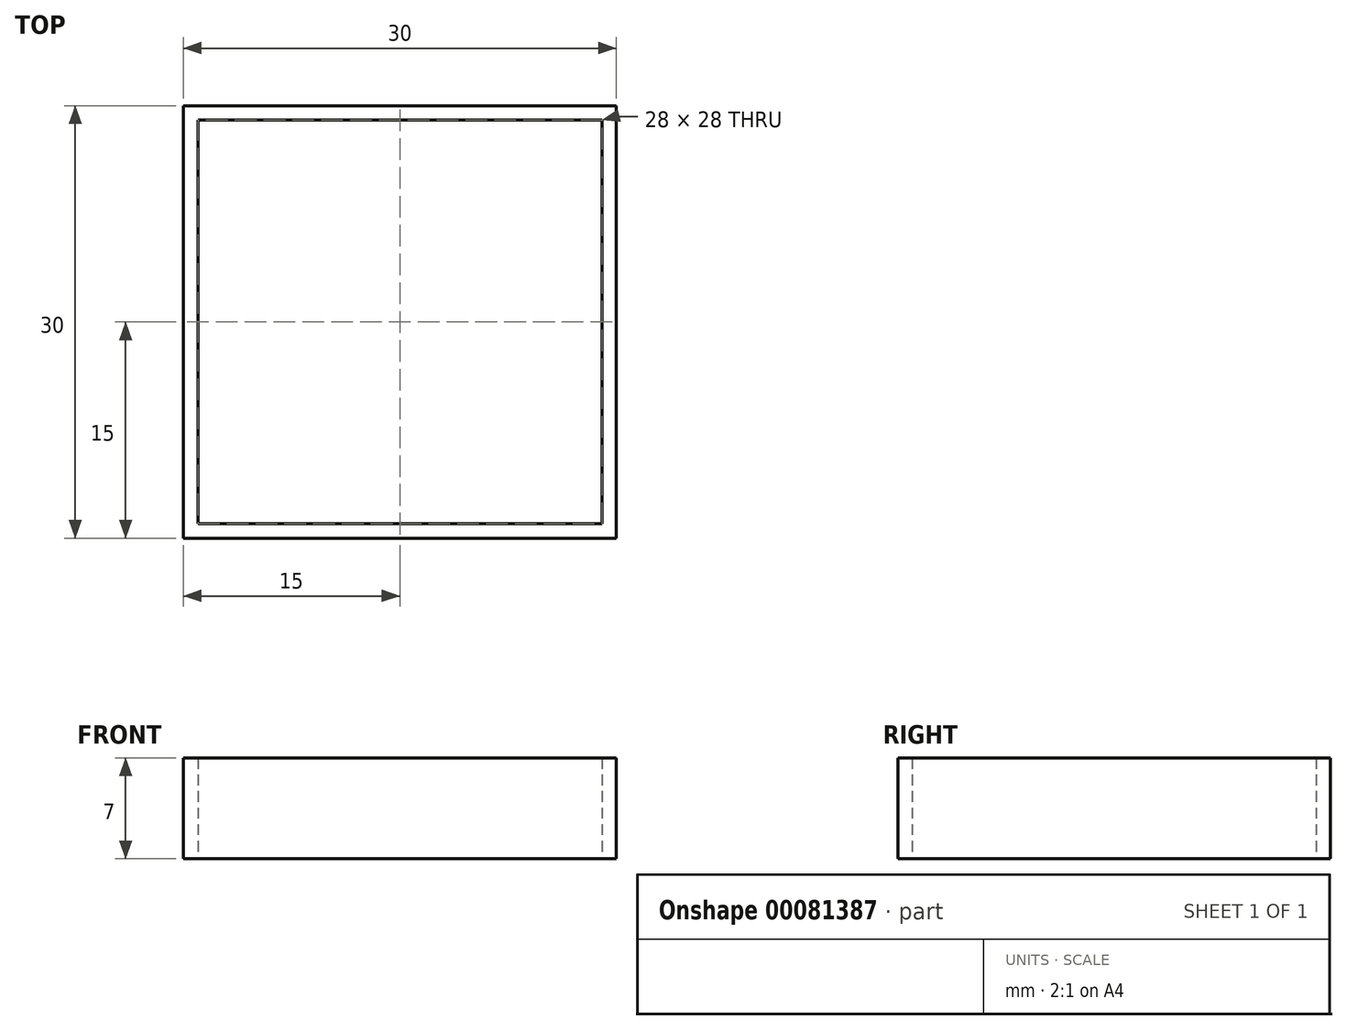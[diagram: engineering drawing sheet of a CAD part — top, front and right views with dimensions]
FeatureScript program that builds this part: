
annotation { "Feature Type Name" : "Feature", "Feature Type Description" : "" }
export const myFeature = defineFeature(function(context is Context, id is Id, definition is map)
    precondition{}
    {
        {
            var Q0;
            Q0=qCreatedBy(makeId("Top.planeOp"),FACE);
            var sketch = newSketch(context, id + "F0", { "sketchPlane" : qUnion([Q0])});
            skLineSegment(sketch, "E0.bottom", {"start": v(15, -15) * mm, "end": v(-15, -15) * mm});
            skLineSegment(sketch, "E0.top", {"start": v(15, 15) * mm, "end": v(-15, 15) * mm});
            skLineSegment(sketch, "E0.left", {"start": v(15, -15) * mm, "end": v(15, 15) * mm});
            skLineSegment(sketch, "E0.right", {"start": v(-15, -15) * mm, "end": v(-15, 15) * mm});
            skPoint(sketch, "E0.middle", {"position": v(0, 0) * mm});
            skLineSegment(sketch, "E1.bottom", {"start": v(14, -14) * mm, "end": v(-14, -14) * mm});
            skLineSegment(sketch, "E1.top", {"start": v(14, 14) * mm, "end": v(-14, 14) * mm});
            skLineSegment(sketch, "E1.left", {"start": v(14, -14) * mm, "end": v(14, 14) * mm});
            skLineSegment(sketch, "E1.right", {"start": v(-14, -14) * mm, "end": v(-14, 14) * mm});
            skSolve(sketch);
        }
        {
            var Q0;
            Q0=makeQuery(id+"F0.imprint","IMPRINT",FACE,{"disambiguationData":[TD([[makeQuery(id+"F0.imprint","IMPRINT",EDGE,{"derivedFrom":sQuery(id+"F0.wireOp",EDGE,"E0.bottom")}),-1.0]])]});
            extrude(context, id + "F1", {"entities" : qUnion([Q0]), "depth" : 7 * mm});
        }
    });
